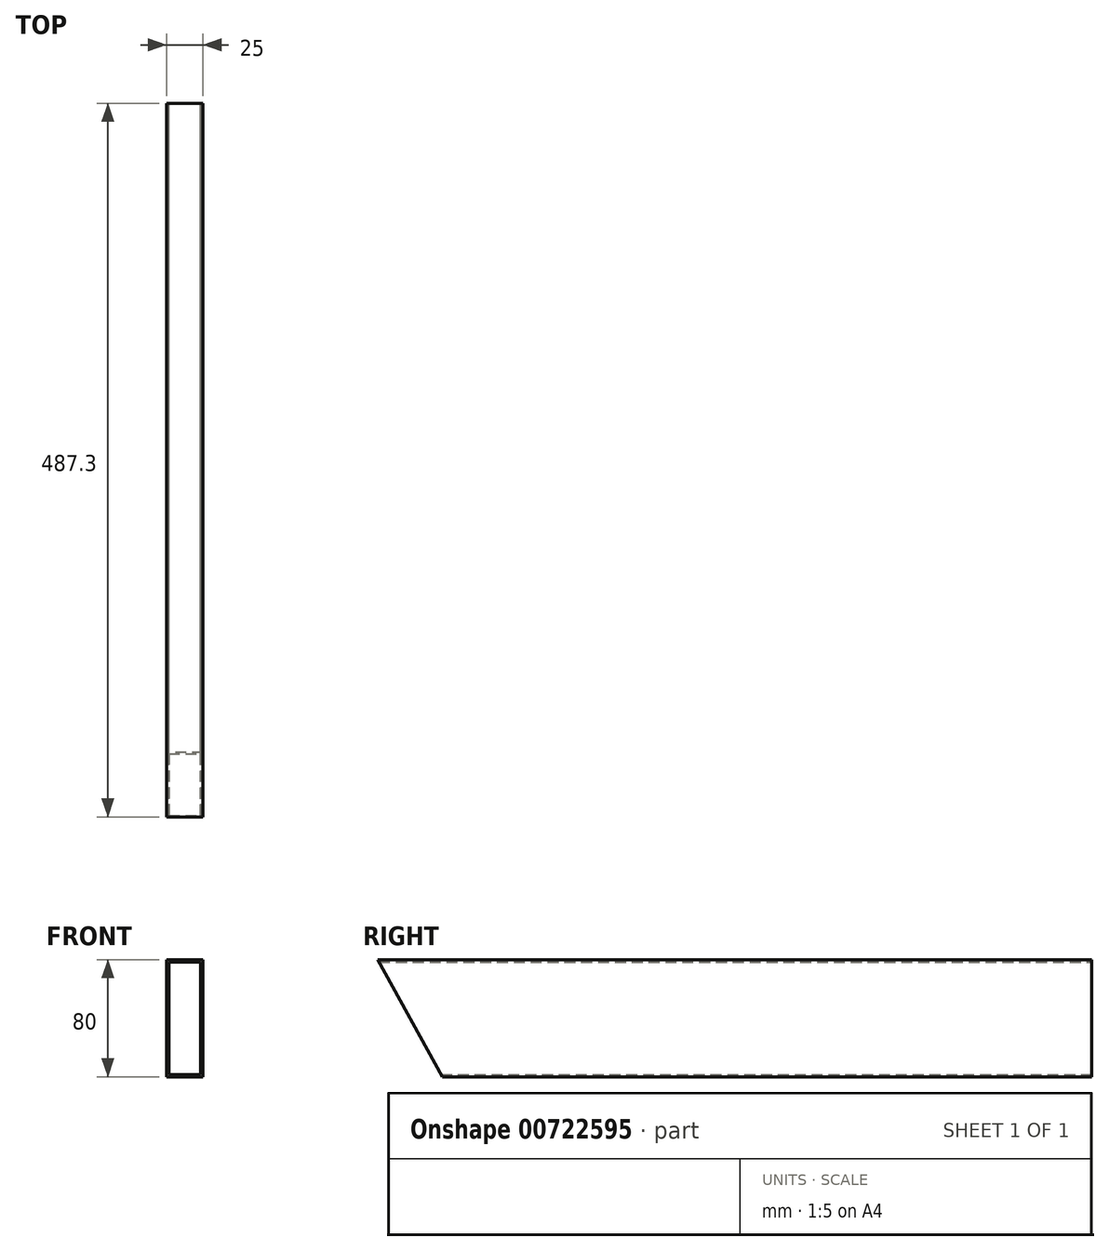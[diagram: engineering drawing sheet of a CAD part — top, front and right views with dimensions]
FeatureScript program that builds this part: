
annotation { "Feature Type Name" : "Feature", "Feature Type Description" : "" }
export const myFeature = defineFeature(function(context is Context, id is Id, definition is map)
    precondition{}
    {
        {
            var Q0;
            Q0=qCreatedBy(makeId("Front.planeOp"),FACE);
            var sketch = newSketch(context, id + "F0", { "sketchPlane" : qUnion([Q0])});
            skLineSegment(sketch, "E0.bottom", {"start": v(-12.5, -40) * mm, "end": v(12.5, -40) * mm});
            skLineSegment(sketch, "E0.top", {"start": v(-12.5, 40) * mm, "end": v(12.5, 40) * mm});
            skLineSegment(sketch, "E0.left", {"start": v(-12.5, -40) * mm, "end": v(-12.5, 40) * mm});
            skLineSegment(sketch, "E0.right", {"start": v(12.5, -40) * mm, "end": v(12.5, 40) * mm});
            skPoint(sketch, "E0.middle", {"position": v(0, 0) * mm});
            skLineSegment(sketch, "E1.bottom", {"start": v(-10.92, -38.41) * mm, "end": v(10.91, -38.41) * mm});
            skLineSegment(sketch, "E1.top", {"start": v(-10.91, 38.41) * mm, "end": v(10.92, 38.41) * mm});
            skLineSegment(sketch, "E1.left", {"start": v(-10.92, -38.41) * mm, "end": v(-10.91, 38.41) * mm});
            skLineSegment(sketch, "E1.right", {"start": v(10.91, -38.41) * mm, "end": v(10.92, 38.41) * mm});
            skSolve(sketch);
        }
        {
            var Q0;
            Q0=makeQuery(id+"F0.imprint","IMPRINT",FACE,{"disambiguationData":[TD([[makeQuery(id+"F0.imprint","IMPRINT",EDGE,{"derivedFrom":sQuery(id+"F0.wireOp",EDGE,"E0.bottom")}),1.0]])]});
            extrude(context, id + "F1", {"entities" : qUnion([Q0]), "endBound" : BoundingType.SYMMETRIC, "depth" : 487.3 * mm, "offsetDistance" : 25 * mm});
        }
        {
            var Q0;
            Q0=makeQuery(id+"F1.opExtrude","CAP_EDGE",EDGE,{"disambiguationData":[OSD([sQuery(id+"F0.wireOp",EDGE,"E0.bottom")])],"isStart":false});
            chamfer(context, id + "F2", {"entities" : qUnion([Q0]), "chamferType" : ChamferType.TWO_OFFSETS, "width1" : 80 * mm, "oppositeDirection" : false, "width2" : 44 * mm, "tangentPropagation" : true});
        }
    });
